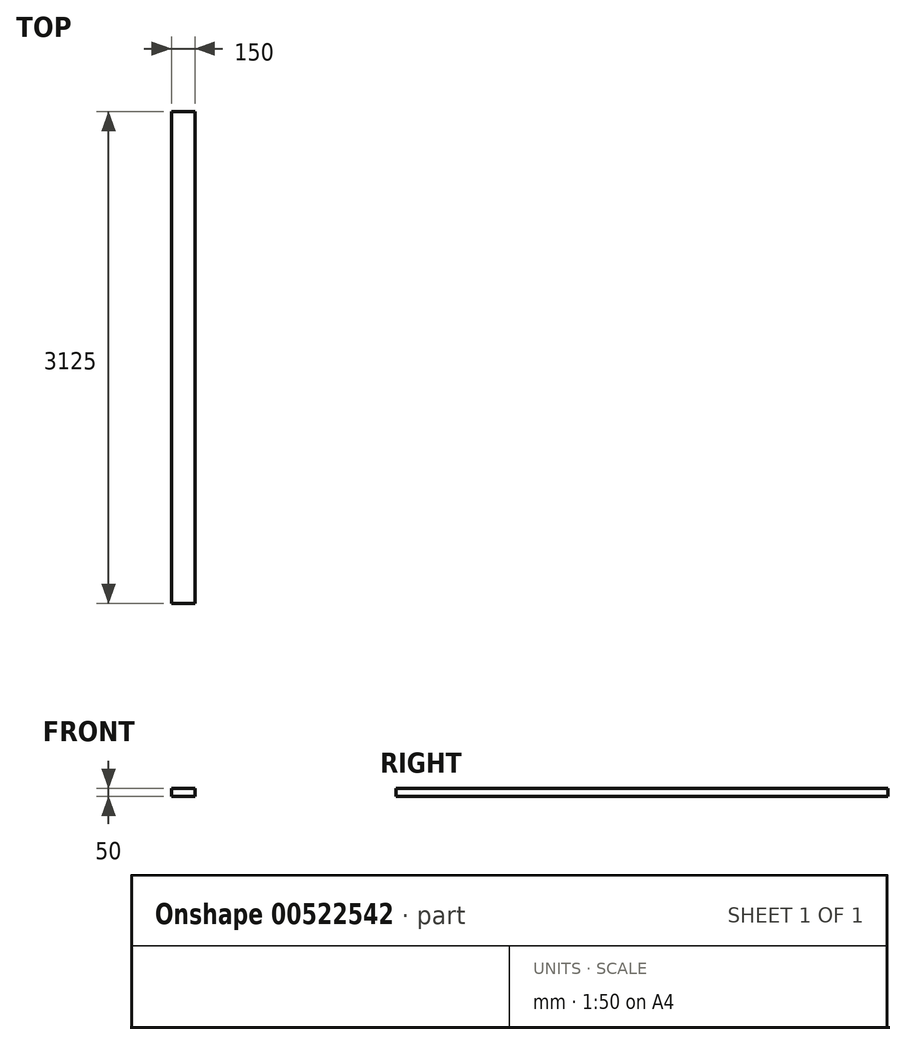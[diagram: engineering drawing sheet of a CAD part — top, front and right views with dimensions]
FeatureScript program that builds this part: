
annotation { "Feature Type Name" : "Feature", "Feature Type Description" : "" }
export const myFeature = defineFeature(function(context is Context, id is Id, definition is map)
    precondition{}
    {
        {
            var Q0;
            Q0=qCreatedBy(makeId("Front.planeOp"),FACE);
            var sketch = newSketch(context, id + "F0", { "sketchPlane" : qUnion([Q0])});
            skLineSegment(sketch, "E0.bottom", {"start": v(-139.39, 44.33) * mm, "end": v(10.61, 44.33) * mm});
            skLineSegment(sketch, "E0.top", {"start": v(-139.39, -5.67) * mm, "end": v(10.61, -5.67) * mm});
            skLineSegment(sketch, "E0.left", {"start": v(-139.39, 44.33) * mm, "end": v(-139.39, -5.67) * mm});
            skLineSegment(sketch, "E0.right", {"start": v(10.61, 44.33) * mm, "end": v(10.61, -5.67) * mm});
            skSolve(sketch);
        }
        {
            var Q0;
            Q0 = qSketchRegion(id + "F0", true);
            extrude(context, id + "F1", {"entities" : qUnion([Q0]), "depth" : 3125 * mm, "offsetDistance" : 25 * mm});
        }
    });
